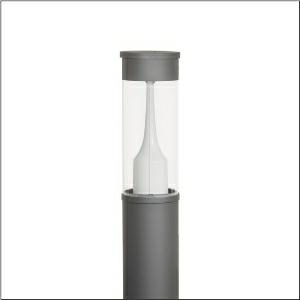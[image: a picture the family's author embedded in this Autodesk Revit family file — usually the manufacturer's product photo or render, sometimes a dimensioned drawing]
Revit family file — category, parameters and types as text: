
# Revit family: city-light_260_iq___p1_0a_5xa5295bf14h_d7c3
name_source: partatom
category: Lighting Fixtures
units: mm (PartAtom-declared; Revit-internal decimal feet)

## family parameters
Cut with Voids When Loaded = No
Host = Face
Light Source = No
Part Type = Normal
Room Calculation Point = No
Round Connector Dimension = Use Diameter
Shared = No

## types (1)
- --- (1 x LED, 1510 lm, 12.9 W, 2200K)
    Apparent Load = 13 VA
    CIE Flux Codes = 32 61 90 93 100
    Color Rendering = 70
    Color Temperature = 2200K
    Default Elevation = 1800 mm
    Description = City-Light 260 iQ, light pillar, Module 540 iQ-SR, primary light control with 3 zone facetted reflector, of plastic, silver coated, highly specular, structured, primary optical cover: cover, of PMMA, transparent, partly coated, light distribution: P1.0a, primary light characteristic: strongly asymmetric, LED, High Power LED, rated luminous flux: 1.510lm, luminous efficacy: 117lm/W, light colour: 722, colour temperature: 2200K, control gear: iQ Street-Remote, control: pre-setting: logarithmic dimming characteristic, Street-Remote, Auto-Match, Temp-Guard, Lumen-Switch, Night-Set, Smart-Wire, Light-Fading, Desk-Remote (wireless, voltage-free reading and setting of iQ features in the workshop via application-optimized NFC function/RFID function), optimised constant luminous flux control (CLO 2.0), with terminal, 6-pole, max. 2.5mm², mains connection: 230..240V, AC, 50/60Hz, start of lifetime: 13W, end of service life: 13W, reduction: 6W, luminaire housing, cylindrical, of extruded aluminium section, coated, Siteco® metallic grey (DB 702S), length: 2.600mm, diameter: 200mm, Module 540 iQ-SR, traffic white (RAL 9016), equipment: standard, protection rating (complete): IP65, insulation class (complete): insulation class II (safety insulation), certification: CE, ENEC, VDE, packaging unit: 1 piece

Light Distribution: P1.0a
    Height = 500 mm
    Lamp = 1 x LED
    Lamp Light Flux = 1510 lm
    Lamp Power = 12.9 W
    Lamp count = 1
    Length = 200 mm  [stored 0.656168 ft]
    Luminous efficacy = 117 lm/W
    Manufacturer = Siteco
    ModVariant = No
    Model = 5XA5295BF14H
    Mounting Place = Floor
    Mounting Type = Freestanding
    Number of Poles = 1
    OnlyDefault = Yes
    Power Factor = 1
    Product Name = City-Light 260 iQ | P1.0a
    Product group = light pillar
    ProductGroupID = 1301
    Protection Class = Protection class II
    Protection Degree = IP 65
    RLX_Detail_Level = 1
    RLX_Emergency_Light_Flux = 0 lm
    RLX_Emergency_Type = 0
    RLX_Emergency_Type_DB = No
    RlxData = <blob elided: 52889 chars, md5=d5467f3c>
    Socket = socket
    Standby Power = 0 W
    System Light Flux = 1510 lm
    System Power = 13 W
    Type Comments = factory setting: luminous flux: 100 % | dim-lin: 254 | 516 mA
    Type Image = l_1006918.jpg
    URL = http://relux.com
    VarID = @adj_159007
    Voltage = 0 V
    Weight = 0.00 kg
    Width = 0 mm  [stored 0 ft]

note: [stored X ft] marks values corroborated as IEEE doubles in the binary element streams (Revit-internal decimal feet)

## geometry (parser evidence)
native form markers: Blend x4, Sweep x10
no freeform markers — native parametric forms only
